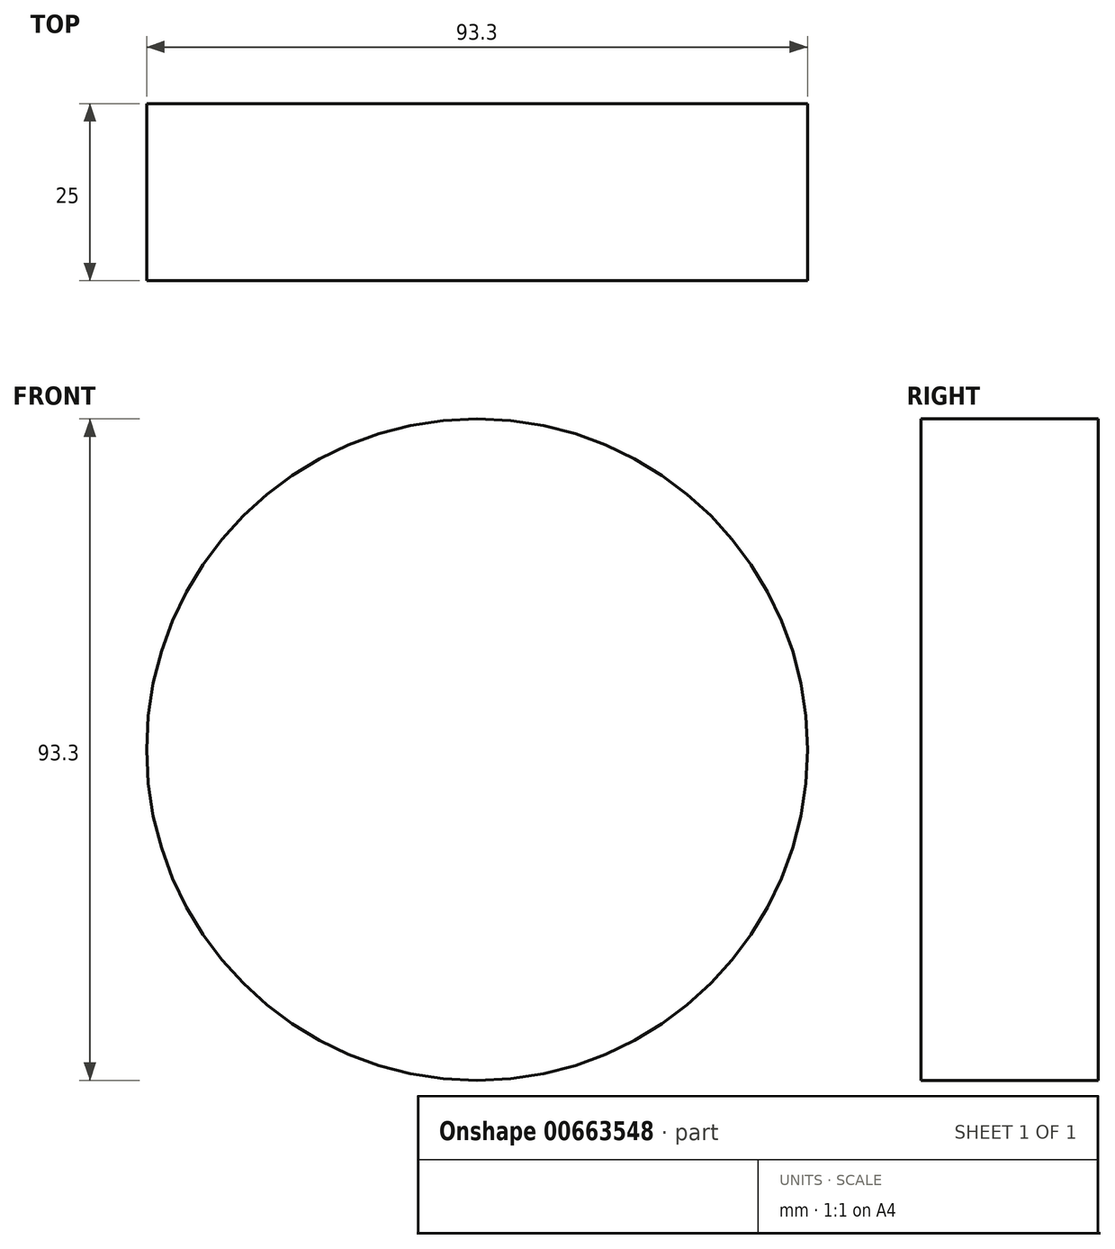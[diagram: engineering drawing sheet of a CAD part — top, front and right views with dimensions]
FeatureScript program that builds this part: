
annotation { "Feature Type Name" : "Feature", "Feature Type Description" : "" }
export const myFeature = defineFeature(function(context is Context, id is Id, definition is map)
    precondition{}
    {
        {
            var Q0;
            Q0=qCreatedBy(makeId("Front.planeOp"),FACE);
            var sketch = newSketch(context, id + "F0", { "sketchPlane" : qUnion([Q0])});
            skCircle(sketch, "E0", {"center": v(0, 0) * mm, "radius": 46.65 * mm});
            skSolve(sketch);
        }
        {
            var Q0;
            Q0 = qSketchRegion(id + "F0", true);
            var Q1;
            Q1=sQuery(id+"F0.wireOp",EDGE,"E0");
            extrude(context, id + "F1", {"entities" : qUnion([Q0]), "bodyType" : ToolBodyType.SURFACE, "surfaceEntities" : qUnion([Q1]), "depth" : 25 * mm, "offsetDistance" : 25 * mm});
        }
    });
